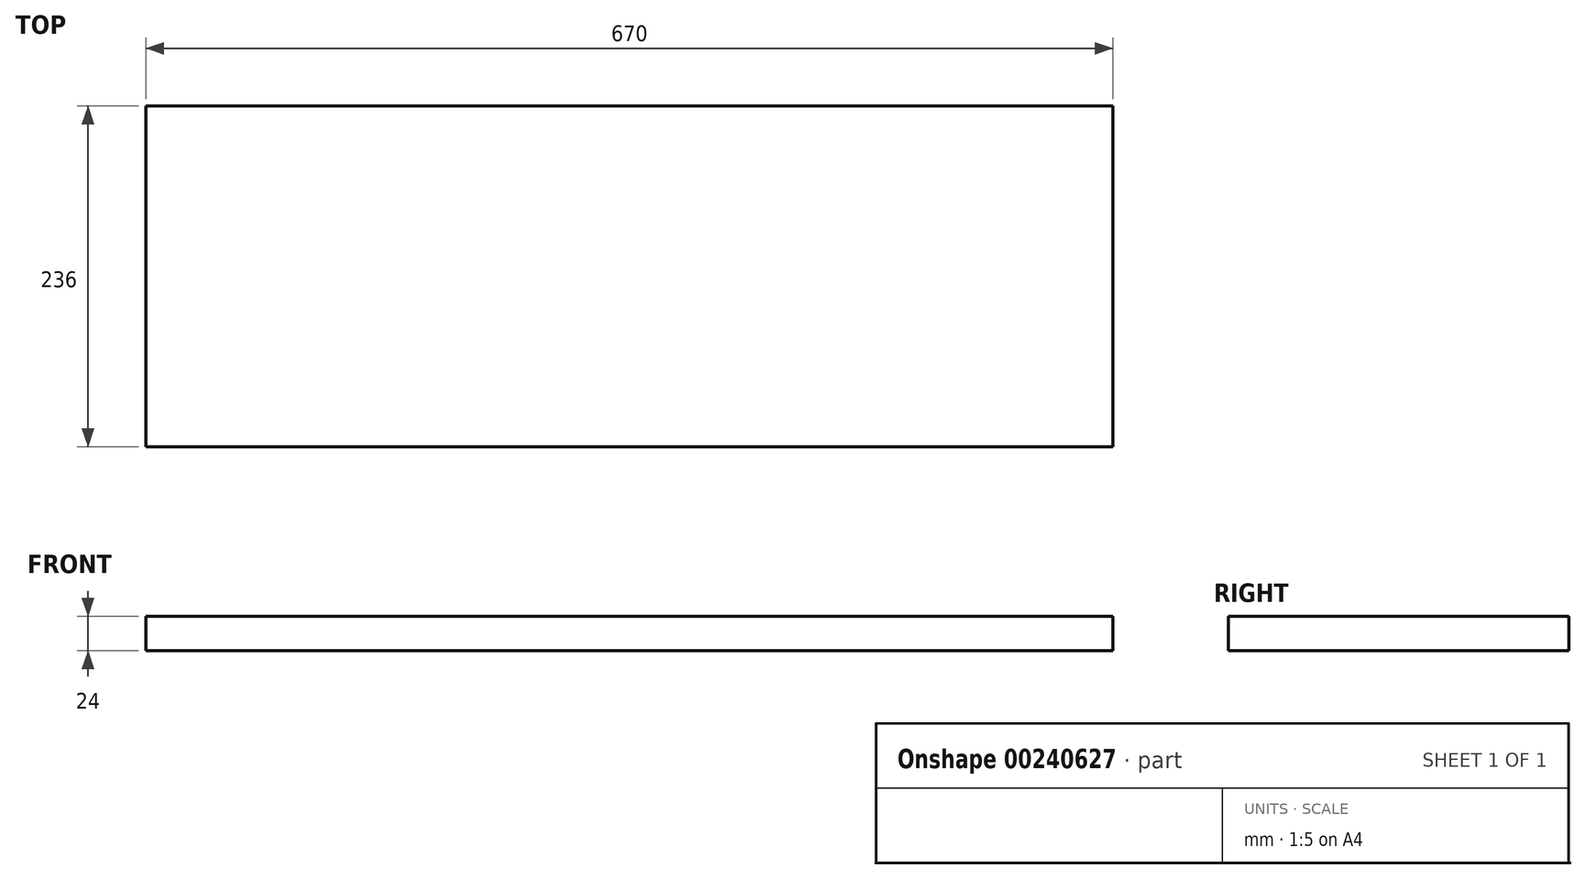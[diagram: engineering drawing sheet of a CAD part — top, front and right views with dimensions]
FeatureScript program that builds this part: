
annotation { "Feature Type Name" : "Feature", "Feature Type Description" : "" }
export const myFeature = defineFeature(function(context is Context, id is Id, definition is map)
    precondition{}
    {
        {
            var Q0;
            Q0=qCreatedBy(makeId("Top.planeOp"),FACE);
            var sketch = newSketch(context, id + "F0", { "sketchPlane" : qUnion([Q0])});
            skLineSegment(sketch, "E0.bottom", {"start": v(-636.65, 224.49) * mm, "end": v(33.35, 224.49) * mm});
            skLineSegment(sketch, "E0.top", {"start": v(-636.65, -11.51) * mm, "end": v(33.35, -11.51) * mm});
            skLineSegment(sketch, "E0.left", {"start": v(-636.65, 224.49) * mm, "end": v(-636.65, -11.51) * mm});
            skLineSegment(sketch, "E0.right", {"start": v(33.35, 224.49) * mm, "end": v(33.35, -11.51) * mm});
            skSolve(sketch);
        }
        {
            var Q0;
            Q0=makeQuery(id+"F0.imprint","IMPRINT",FACE,{"disambiguationData":[TD([[makeQuery(id+"F0.imprint","IMPRINT",EDGE,{"derivedFrom":sQuery(id+"F0.wireOp",EDGE,"E0.bottom")}),-1.0]])]});
            extrude(context, id + "F1", {"entities" : qUnion([Q0]), "depth" : 24 * mm});
        }
    });
